# Revit family: Seating-LAMMHULTS-CAMPUS-Armchair_Sledbase
name_source: partatom
category: Furniture
revit_build: Autodesk Revit Architecture 2012 (Build: 20110916_2132(x64)
units: mm (PartAtom-declared; Revit-internal decimal feet)

## types (5) — shared parameters
Armrest Material = Plastic - Black
Assembly Code = E2020
Description = *Please enter mtrl description here for use in mto*
Frame Material = Metal - Chrome - Polished
Keynote = 46.B
Manufacturer = LAMMHULTS
Model = CAMPUS
URL = www.lammhults.se

## per-type parameters (varying)
| type | Back Material | Seat Material |
| Fabric-Red | Fabric - Red | Fabric - Red |
| Laminate-White | Laminate - Compact - White | Laminate - Compact - White |
| Laminate-Black | Laminate - Compact - Black | Laminate - Compact - Black |
| Wood-Oak | Wood - Veneer - Oak | Wood - Veneer - Oak |
| Wood-Birch | Wood - Veneer - Birch | Wood - Veneer - Birch |

## geometry (parser evidence)
native form markers: Blend x12, Sweep x1
no freeform markers — native parametric forms only
